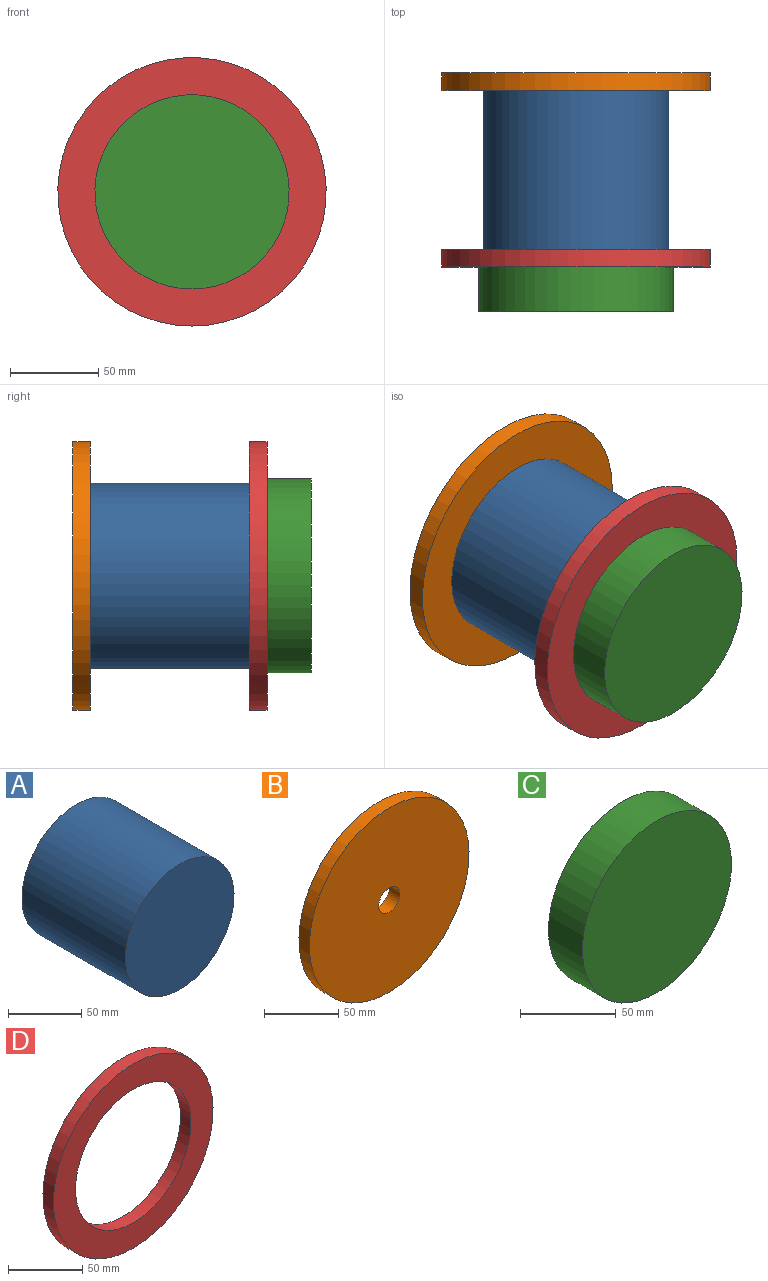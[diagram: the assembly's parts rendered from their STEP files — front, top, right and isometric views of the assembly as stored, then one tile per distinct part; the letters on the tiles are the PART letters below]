
ASSEMBLY  parts=4 mates=3
PART A: 3 faces, bbox 105x100x105 mm
  f0: cylinder r=52.5mm len=105mm, axis (0,1,0), area 32986.7mm2, adj f1,f2
  f1: plane 105x105mm, normal (0,-1,0), area 8659mm2, adj f0
  f2: plane 105x105mm, normal (0,1,0), area 8659mm2, adj f0
PART B: 4 faces, bbox 152x10x152 mm
  f0: cylinder r=10mm len=20mm, axis (0,1,0), area 628.3mm2, adj f2,f3
  f1: cylinder r=76mm len=152mm, axis (0,1,0), area 4775.2mm2, adj f2,f3
  f2: plane 152x152mm, normal (0,-1,0), area 17831.7mm2, adj f0,f1
  f3: plane 152x152mm, normal (0,1,0), area 17831.7mm2, adj f0,f1
PART C: 5 faces, bbox 110x25x110 mm
  f0: cylinder r=55mm len=110mm, axis (0,1,0), area 8639.4mm2, adj f1,f2
  f1: plane 110x110mm, normal (0,-1,0), area 9503.3mm2, adj f0
  f2: plane 110x110mm, normal (0,1,0), area 678.6mm2, adj f0,f3
  f3: cylinder r=53mm len=106mm, axis (0,1,0), area 7659.2mm2, adj f2,f4
  f4: plane 106x106mm, normal (0,1,0), area 8824.7mm2, adj f3
PART D: 4 faces, bbox 152x10x152 mm
  f0: cylinder r=55mm len=110mm, axis (0,1,0), area 3455.8mm2, adj f2,f3
  f1: cylinder r=76mm len=152mm, axis (0,1,0), area 4775.2mm2, adj f2,f3
  f2: plane 152x152mm, normal (0,-1,0), area 8642.5mm2, adj f0,f1
  f3: plane 152x152mm, normal (0,1,0), area 8642.5mm2, adj f0,f1
PLACE A t=(68.21,63.77,-25.99)mm
PLACE B t=(68.21,73.77,-25.99)mm
PLACE C t=(68.21,-36.23,-25.99)mm
PLACE D t=(68.21,-26.23,-25.99)mm
MATE fastened A.f0 <-> C.f0  axis (0,-1,0) through (68.21,-36.23,-25.99)mm
MATE fastened D.f0 <-> C.f0  axis (0,-1,0) through (68.21,-36.23,-25.99)mm
MATE fastened B.f1 <-> A.f0  axis (0,-1,0) through (68.21,63.77,-25.99)mm
